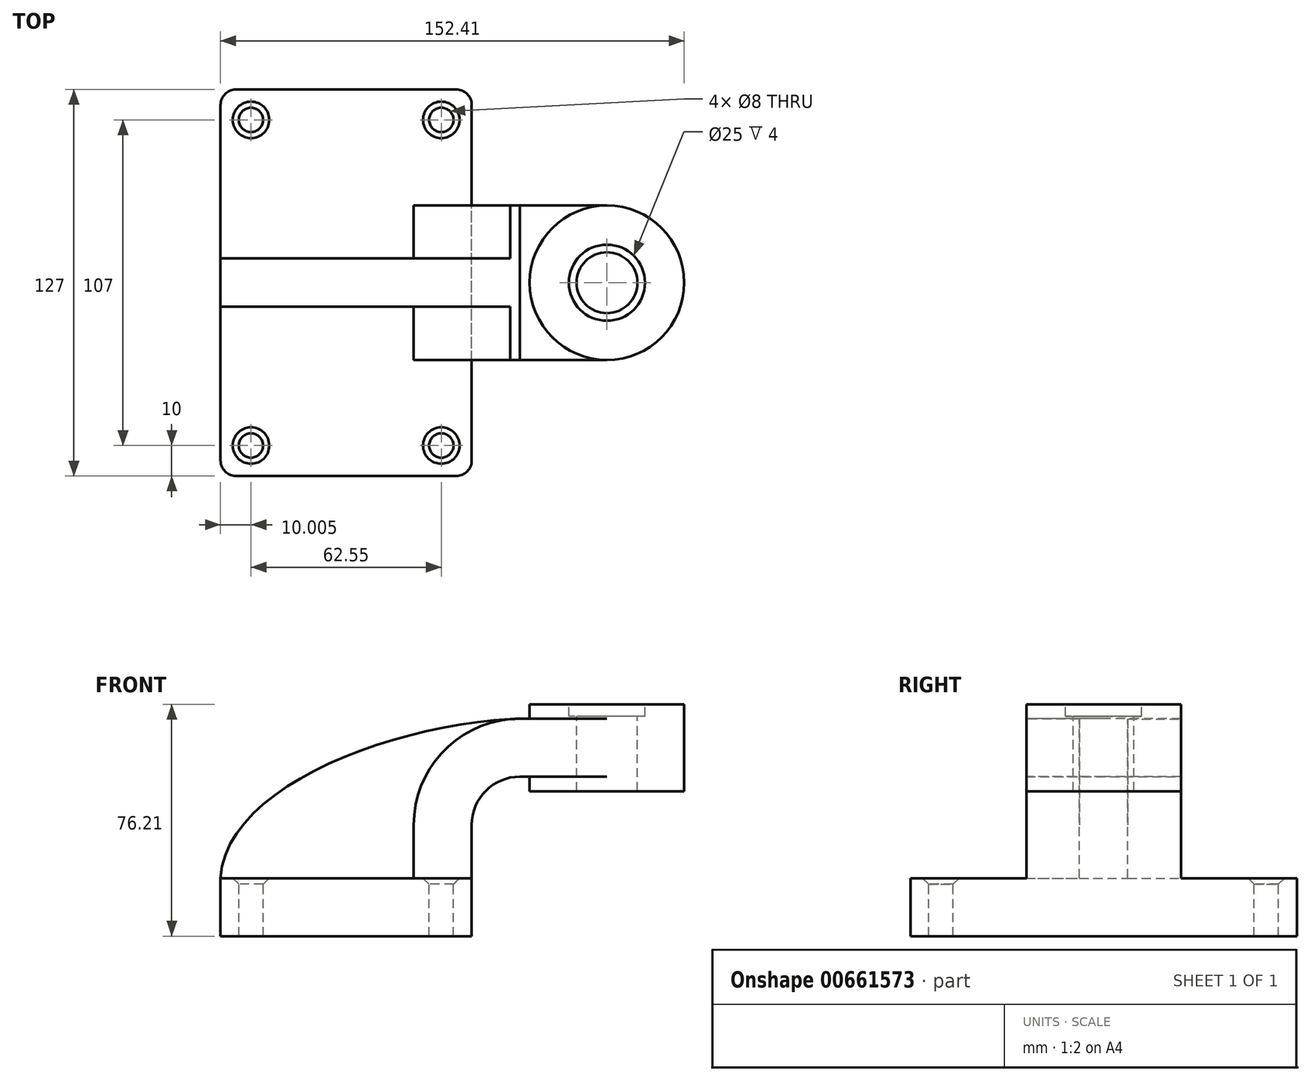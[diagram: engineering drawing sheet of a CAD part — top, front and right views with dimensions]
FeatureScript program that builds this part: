
annotation { "Feature Type Name" : "Feature", "Feature Type Description" : "" }
export const myFeature = defineFeature(function(context is Context, id is Id, definition is map)
    precondition{}
    {
        {
            var Q0;
            Q0=qCreatedBy(makeId("Front.planeOp"),FACE);
            var sketch = newSketch(context, id + "F0", { "sketchPlane" : qUnion([Q0])});
            skLineSegment(sketch, "E0.rect.bottom", {"start": v(-41.28, 9.52) * mm, "end": v(41.28, 9.52) * mm});
            skLineSegment(sketch, "E0.rect.top", {"start": v(-41.28, -9.52) * mm, "end": v(41.28, -9.52) * mm});
            skLineSegment(sketch, "E0.rect.left", {"start": v(-41.28, 9.52) * mm, "end": v(-41.28, -9.52) * mm});
            skLineSegment(sketch, "E0.rect.right", {"start": v(41.28, 9.52) * mm, "end": v(41.28, -9.52) * mm});
            skPoint(sketch, "E0.rect.middle", {"position": v(0, 0) * mm});
            skLineSegment(sketch, "E1", {"start": v(41.28, 9.52) * mm, "end": v(41.28, 27) * mm});
            skArc(sketch, "E2", {"start": v(41.28, 27) * mm, "mid": v(45.92, 38.23) * mm, "end": v(57.15, 42.88) * mm});
            skLineSegment(sketch, "E3", {"start": v(57.15, 42.88) * mm, "end": v(85.72, 42.88) * mm});
            skLineSegment(sketch, "E4.rect.bottom", {"start": v(60.32, 38.1) * mm, "end": v(111.12, 38.1) * mm});
            skLineSegment(sketch, "E4.rect.top", {"start": v(60.32, 66.68) * mm, "end": v(111.12, 66.68) * mm});
            skLineSegment(sketch, "E4.rect.left", {"start": v(60.32, 38.1) * mm, "end": v(60.32, 66.68) * mm});
            skLineSegment(sketch, "E4.rect.right", {"start": v(111.13, 38.1) * mm, "end": v(111.12, 66.68) * mm});
            skPoint(sketch, "E4.rect.middle", {"position": v(85.72, 52.39) * mm});
            skLineSegment(sketch, "E5.0", {"start": v(57.15, 61.93) * mm, "end": v(85.72, 61.93) * mm});
            skArc(sketch, "E5.1", {"start": v(22.23, 27) * mm, "mid": v(32.45, 51.7) * mm, "end": v(57.15, 61.93) * mm});
            skLineSegment(sketch, "E5.2", {"start": v(22.23, 9.52) * mm, "end": v(22.23, 27) * mm});
            skLineSegment(sketch, "E6", {"start": v(85.72, 38.1) * mm, "end": v(85.72, 66.68) * mm});
            skFitSpline(sketch, "E7", {"points": [v(-41.28, 9.53) * mm, v(57.15, 61.93) * mm], "startDerivative": vector(5.2, 92.34) * mm, "endDerivative": vector(120.92, 4.22) * mm});
            skSolve(sketch);
        }
        {
            var Q0;
            Q0=makeQuery(id+"F0.imprint","IMPRINT",FACE,{"disambiguationData":[TD([[makeQuery(id+"F0.imprint","IMPRINT",EDGE,{"derivedFrom":sQuery(id+"F0.wireOp",EDGE,"E0.rect.top")}),1.0]])]});
            extrude(context, id + "F1", {"entities" : qUnion([Q0]), "endBound" : BoundingType.SYMMETRIC, "depth" : 127 * mm});
        }
        {
            var Q0;
            {var subQ9=sQuery(id+"F0.wireOp",EDGE,"E1");Q0=makeQuery(id+"F0.imprint","IMPRINT",FACE,{"disambiguationData":[TD([[makeQuery(id+"F0.imprint","IMPRINT",EDGE,{"derivedFrom":subQ9}),1.0]])]});}
            var Q1;
            {var subQ0=sQuery(id+"F0.wireOp",EDGE,"E6");var subQ1=sQuery(id+"F0.wireOp",EDGE,"E3");var subQ2=makeQuery(id+"F0.imprint","INTERSECT",VERTEX,{"derivedFrom":[subQ1,subQ0]});Q1=makeQuery(id+"F0.imprint","IMPRINT",FACE,{"disambiguationData":[TD([[makeQuery(id+"F0.imprint","IMPRINT",EDGE,{"disambiguationData":[TD([[subQ2,1.0]])],"derivedFrom":subQ1}),1.0]])]});}
            extrude(context, id + "F2", {"entities" : qUnion([Q0, Q1]), "operationType" : NewBodyOperationType.ADD, "endBound" : BoundingType.SYMMETRIC, "depth" : 50.8 * mm});
        }
        {
            var Q0;
            {var subQ3=sQuery(id+"F0.wireOp",EDGE,"E5.2");Q0=makeQuery(id+"F0.imprint","IMPRINT",FACE,{"disambiguationData":[TD([[makeQuery(id+"F0.imprint","IMPRINT",EDGE,{"derivedFrom":subQ3}),1.0]])]});}
            extrude(context, id + "F3", {"entities" : qUnion([Q0]), "operationType" : NewBodyOperationType.ADD, "endBound" : BoundingType.SYMMETRIC, "depth" : 15.88 * mm});
        }
        {
            var Q0;
            {var subQ5=sQuery(id+"F0.wireOp",EDGE,"E4.rect.right");Q0=makeQuery(id+"F0.imprint","IMPRINT",FACE,{"disambiguationData":[TD([[makeQuery(id+"F0.imprint","IMPRINT",EDGE,{"derivedFrom":subQ5}),1.0]])]});}
            var Q1;
            Q1=sQuery(id+"F0.wireOp",EDGE,"E6");
            revolve(context, id + "F4", {"operationType" : NewBodyOperationType.ADD, "entities" : qUnion([Q0]), "axis" : qUnion([Q1]), "revolveType" : RevolveType.FULL});
        }
        {
            var Q0;
            Q0=makeQuery(id+"F1.opExtrude","CAP_EDGE",EDGE,{"disambiguationData":[OSD([sQuery(id+"F0.wireOp",EDGE,"E0.rect.right")])],"isStart":false});
            var Q1;
            Q1=makeQuery(id+"F1.opExtrude","CAP_EDGE",EDGE,{"disambiguationData":[OSD([sQuery(id+"F0.wireOp",EDGE,"E0.rect.left")])],"isStart":false});
            var Q2;
            Q2=makeQuery(id+"F1.opExtrude","CAP_EDGE",EDGE,{"disambiguationData":[OSD([sQuery(id+"F0.wireOp",EDGE,"E0.rect.right")])],"isStart":true});
            var Q3;
            Q3=makeQuery(id+"F1.opExtrude","CAP_EDGE",EDGE,{"disambiguationData":[OSD([sQuery(id+"F0.wireOp",EDGE,"E0.rect.left")])],"isStart":true});
            fillet(context, id + "F5", {"entities" : qUnion([Q0, Q1, Q2, Q3]), "radius" : 5.08 * mm, "tangentPropagation" : true, "allowEdgeOverflow" : false});
        }
        {
            var Q0;
            Q0=makeQuery(id+"F4.opRevolve","SWEPT_FACE",FACE,{"disambiguationData":[OSD([sQuery(id+"F0.wireOp",EDGE,"E4.rect.top")])]});
            var sketch = newSketch(context, id + "F6", { "sketchPlane" : qUnion([Q0])});
            skCircle(sketch, "E8", {"center": v(85.72, 0) * mm, "radius": 12.49 * mm});
            skSolve(sketch);
        }
        {
            var Q0;
            Q0=sQuery(id+"F6.wireOp",VERTEX,"E8.center");
            var Q1;
            Q1=makeQuery(id+"F1.opExtrude","SWEPT_BODY",BODY,{"disambiguationData":[OSD([sQuery(id+"F0.wireOp",EDGE,"E0.rect.bottom"),sQuery(id+"F0.wireOp",EDGE,"E0.rect.top"),sQuery(id+"F0.wireOp",EDGE,"E0.rect.left"),sQuery(id+"F0.wireOp",EDGE,"E0.rect.right")])]});
            hole(context, id + "F7", {"style" : HoleStyle.C_BORE, "endStyle" : HoleEndStyle.THROUGH, "holeDiameter" : 20 * mm, "cBoreDiameter" : 25 * mm, "cBoreDepth" : 4 * mm, "majorDiameter" : 5 * mm, "isTappedThrough" : true, "tappedDepth" : 12.7 * mm, "tapClearance" : 3, "locations" : qUnion([Q0]), "scope" : qUnion([Q1])});
        }
        {
            var Q0;
            {var subQ4=sQuery(id+"F0.wireOp",EDGE,"E0.rect.bottom");var subQ5=sQuery(id+"F0.wireOp",EDGE,"E0.rect.right");var subQ6=sQuery(id+"F0.wireOp",EDGE,"E0.rect.left");Q0=makeQuery(id+"F3.boolean.opBoolean","SPLIT",FACE,{"disambiguationData":[TD([makeQuery(id+"F1.opExtrude","CAP_FACE",FACE,{"disambiguationData":[OSD([subQ4,sQuery(id+"F0.wireOp",EDGE,"E0.rect.top"),subQ6,subQ5])],"isStart":true})])],"derivedFrom":makeQuery(id+"F1.opExtrude","SWEPT_FACE",FACE,{"disambiguationData":[OSD([subQ4])]})});}
            var sketch = newSketch(context, id + "F8", { "sketchPlane" : qUnion([Q0])});
            skCircle(sketch, "E9", {"center": v(-31.28, 53.5) * mm, "radius": 5 * mm});
            skCircle(sketch, "E10", {"center": v(31.28, 53.5) * mm, "radius": 5 * mm});
            skCircle(sketch, "E11", {"center": v(-31.28, -53.5) * mm, "radius": 5 * mm});
            skCircle(sketch, "E12", {"center": v(31.28, -53.5) * mm, "radius": 5 * mm});
            skSolve(sketch);
        }
        {
            var Q0;
            Q0=sQuery(id+"F8.wireOp",VERTEX,"E9.center");
            var Q1;
            Q1=sQuery(id+"F8.wireOp",VERTEX,"E10.center");
            var Q2;
            Q2=sQuery(id+"F8.wireOp",VERTEX,"E12.center");
            var Q3;
            Q3=sQuery(id+"F8.wireOp",VERTEX,"E11.center");
            var Q4;
            Q4=makeQuery(id+"F1.opExtrude","SWEPT_BODY",BODY,{"disambiguationData":[OSD([sQuery(id+"F0.wireOp",EDGE,"E0.rect.bottom"),sQuery(id+"F0.wireOp",EDGE,"E0.rect.top"),sQuery(id+"F0.wireOp",EDGE,"E0.rect.left"),sQuery(id+"F0.wireOp",EDGE,"E0.rect.right")])]});
            hole(context, id + "F9", {"style" : HoleStyle.C_SINK, "endStyle" : HoleEndStyle.THROUGH, "holeDiameter" : 8 * mm, "cSinkDiameter" : 12 * mm, "cSinkAngle" : 90 * degree, "majorDiameter" : 5 * mm, "isTappedThrough" : true, "tappedDepth" : 12.7 * mm, "tapClearance" : 3, "locations" : qUnion([Q0, Q1, Q2, Q3]), "scope" : qUnion([Q4])});
        }
    });
